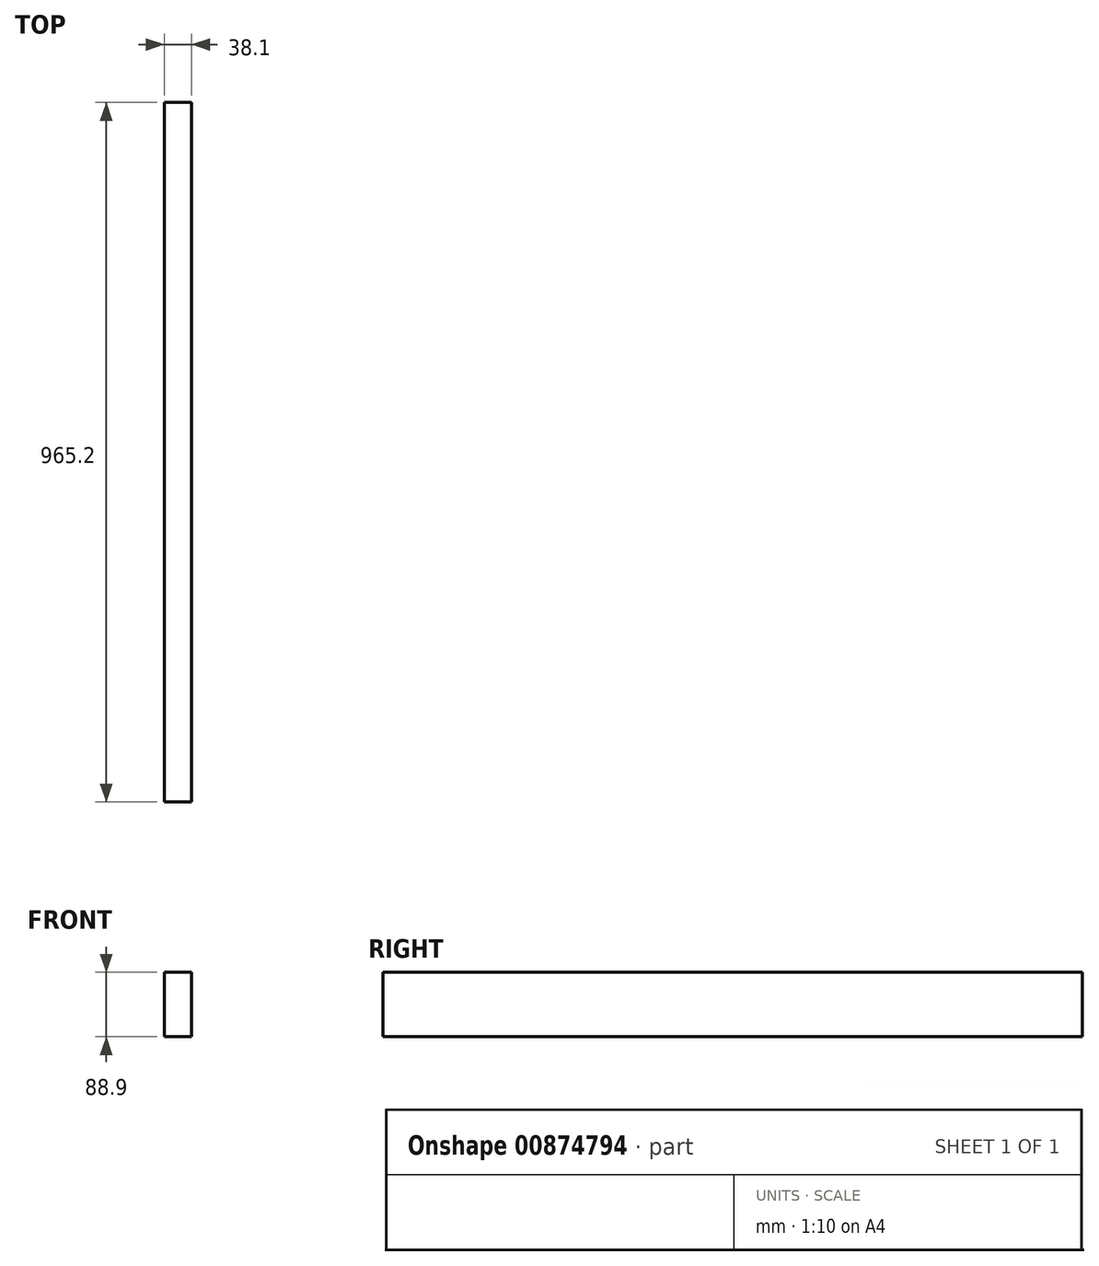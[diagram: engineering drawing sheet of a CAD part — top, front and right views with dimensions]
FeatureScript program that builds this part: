
annotation { "Feature Type Name" : "Feature", "Feature Type Description" : "" }
export const myFeature = defineFeature(function(context is Context, id is Id, definition is map)
    precondition{}
    {
        {
            var Q0;
            Q0=qCreatedBy(makeId("Front.planeOp"),FACE);
            var sketch = newSketch(context, id + "F0", { "sketchPlane" : qUnion([Q0])});
            skLineSegment(sketch, "E0.bottom", {"start": v(-19.05, 44.45) * mm, "end": v(19.05, 44.45) * mm});
            skLineSegment(sketch, "E0.top", {"start": v(-19.05, -44.45) * mm, "end": v(19.05, -44.45) * mm});
            skLineSegment(sketch, "E0.left", {"start": v(-19.05, 44.45) * mm, "end": v(-19.05, -44.45) * mm});
            skLineSegment(sketch, "E0.right", {"start": v(19.05, 44.45) * mm, "end": v(19.05, -44.45) * mm});
            skPoint(sketch, "E0.middle", {"position": v(0, 0) * mm});
            skSolve(sketch);
        }
        {
            var Q0;
            Q0 = qSketchRegion(id + "F0", true);
            extrude(context, id + "F1", {"entities" : qUnion([Q0]), "depth" : 965.2 * mm, "offsetDistance" : 25.4 * mm});
        }
    });
